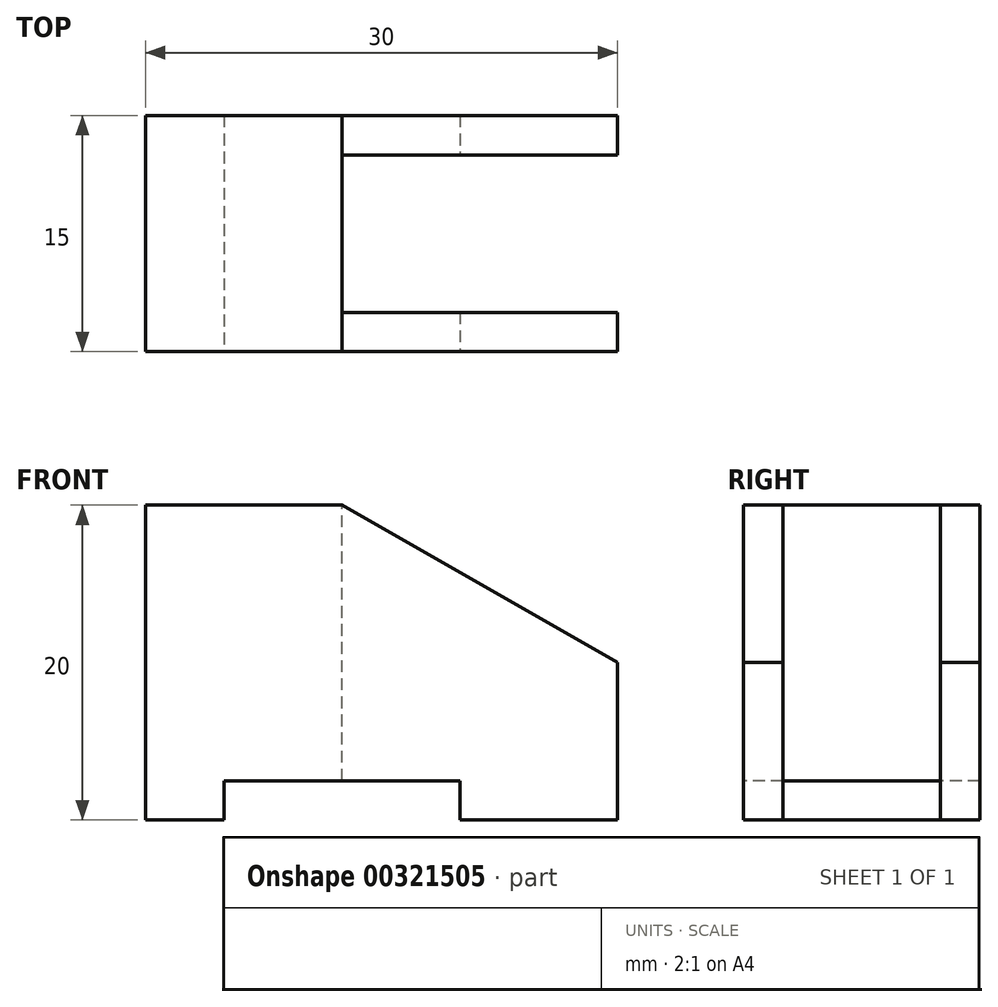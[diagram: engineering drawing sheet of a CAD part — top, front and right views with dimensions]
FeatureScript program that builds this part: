
annotation { "Feature Type Name" : "Feature", "Feature Type Description" : "" }
export const myFeature = defineFeature(function(context is Context, id is Id, definition is map)
    precondition{}
    {
        {
            var Q0;
            Q0=qCreatedBy(makeId("Front.planeOp"),FACE);
            var sketch = newSketch(context, id + "F0", { "sketchPlane" : qUnion([Q0])});
            skLineSegment(sketch, "E0.bottom", {"start": v(0, 0) * mm, "end": v(12.5, 0) * mm});
            skLineSegment(sketch, "E0.top", {"start": v(0, 20) * mm, "end": v(12.5, 20) * mm});
            skLineSegment(sketch, "E0.left", {"start": v(0, 0) * mm, "end": v(0, 20) * mm});
            skLineSegment(sketch, "E0.right", {"start": v(12.5, 0) * mm, "end": v(12.5, 20) * mm});
            skSolve(sketch);
        }
        {
            var Q0;
            Q0 = qSketchRegion(id + "F0", true);
            extrude(context, id + "F1", {"entities" : qUnion([Q0]), "endBound" : BoundingType.SYMMETRIC, "depth" : 15 * mm});
        }
        {
            var Q0;
            Q0=makeQuery(id+"F1.opExtrude","CAP_FACE",FACE,{"disambiguationData":[OSD([sQuery(id+"F0.wireOp",EDGE,"E0.bottom"),sQuery(id+"F0.wireOp",EDGE,"E0.top"),sQuery(id+"F0.wireOp",EDGE,"E0.left"),sQuery(id+"F0.wireOp",EDGE,"E0.right")])],"isStart":false});
            var sketch = newSketch(context, id + "F2", { "sketchPlane" : qUnion([Q0])});
            skLineSegment(sketch, "E1", {"start": v(12.5, 0) * mm, "end": v(30, 0) * mm});
            skLineSegment(sketch, "E2", {"start": v(30, 0) * mm, "end": v(30, 10) * mm});
            skLineSegment(sketch, "E3", {"start": v(30, 10) * mm, "end": v(12.5, 20) * mm});
            skSolve(sketch);
        }
        {
            var Q0;
            Q0 = qSketchRegion(id + "F2", true);
            var Q1;
            Q1=makeQuery(id+"F2.imprint","IMPRINT",FACE,{"disambiguationData":[TD([[makeQuery(id+"F2.imprint","IMPRINT",EDGE,{"derivedFrom":sQuery(id+"F2.wireOp",EDGE,"E1")}),1.0]])]});
            extrude(context, id + "F3", {"entities" : qUnion([Q0, Q1]), "operationType" : NewBodyOperationType.ADD, "oppositeDirection" : true, "depth" : 2.5 * mm});
        }
        {
            var Q0;
            Q0=makeQuery(id+"F1.opExtrude","CAP_FACE",FACE,{"disambiguationData":[OSD([sQuery(id+"F0.wireOp",EDGE,"E0.bottom"),sQuery(id+"F0.wireOp",EDGE,"E0.top"),sQuery(id+"F0.wireOp",EDGE,"E0.left"),sQuery(id+"F0.wireOp",EDGE,"E0.right")])],"isStart":true});
            var sketch = newSketch(context, id + "F4", { "sketchPlane" : qUnion([Q0])});
            skLineSegment(sketch, "E4", {"start": v(-12.5, 0) * mm, "end": v(-30, 0) * mm});
            skLineSegment(sketch, "E5", {"start": v(-30, 0) * mm, "end": v(-30, 10) * mm});
            skLineSegment(sketch, "E6", {"start": v(-30, 10) * mm, "end": v(-12.5, 20) * mm});
            skLineSegment(sketch, "E7", {"start": v(-12.5, 20) * mm, "end": v(-12.5, 0) * mm});
            skSolve(sketch);
        }
        {
            var Q0;
            Q0=makeQuery(id+"F4.imprint","IMPRINT",FACE,{"disambiguationData":[TD([[makeQuery(id+"F4.imprint","IMPRINT",EDGE,{"derivedFrom":sQuery(id+"F4.wireOp",EDGE,"E4")}),-1.0]])]});
            extrude(context, id + "F5", {"entities" : qUnion([Q0]), "operationType" : NewBodyOperationType.ADD, "oppositeDirection" : true, "depth" : 2.5 * mm});
        }
        {
            var Q0;
            {var subQ0=sQuery(id+"F0.wireOp",EDGE,"E0.right");Q0=makeQuery(id+"F3.boolean.opBoolean","MERGE",FACE,{"derivedFrom":[makeQuery(id+"F1.opExtrude","CAP_FACE",FACE,{"disambiguationData":[OSD([sQuery(id+"F0.wireOp",EDGE,"E0.bottom"),sQuery(id+"F0.wireOp",EDGE,"E0.top"),sQuery(id+"F0.wireOp",EDGE,"E0.left"),subQ0])],"isStart":false}),makeQuery(id+"F3.opExtrude","CAP_FACE",FACE,{"disambiguationData":[OSD([subQ0,sQuery(id+"F2.wireOp",EDGE,"E1"),sQuery(id+"F2.wireOp",EDGE,"E2"),sQuery(id+"F2.wireOp",EDGE,"E3")])],"isStart":true})]});}
            var sketch = newSketch(context, id + "F6", { "sketchPlane" : qUnion([Q0])});
            skLineSegment(sketch, "E8.bottom", {"start": v(5, 0) * mm, "end": v(20, 0) * mm});
            skLineSegment(sketch, "E8.top", {"start": v(5, 2.5) * mm, "end": v(20, 2.5) * mm});
            skLineSegment(sketch, "E8.left", {"start": v(5, 0) * mm, "end": v(5, 2.5) * mm});
            skLineSegment(sketch, "E8.right", {"start": v(20, 0) * mm, "end": v(20, 2.5) * mm});
            skSolve(sketch);
        }
        {
            var Q0;
            Q0=makeQuery(id+"F6.imprint","IMPRINT",FACE,{"disambiguationData":[TD([[makeQuery(id+"F6.imprint","IMPRINT",EDGE,{"derivedFrom":sQuery(id+"F6.wireOp",EDGE,"E8.bottom")}),1.0]])]});
            var Q1;
            Q1=makeQuery(id+"F5.boolean.opBoolean","MERGE",FACE,{"derivedFrom":[makeQuery(id+"F1.opExtrude","CAP_FACE",FACE,{"disambiguationData":[OSD([sQuery(id+"F0.wireOp",EDGE,"E0.bottom"),sQuery(id+"F0.wireOp",EDGE,"E0.top"),sQuery(id+"F0.wireOp",EDGE,"E0.left"),sQuery(id+"F0.wireOp",EDGE,"E0.right")])],"isStart":true}),makeQuery(id+"F5.opExtrude","CAP_FACE",FACE,{"disambiguationData":[OSD([sQuery(id+"F4.wireOp",EDGE,"E4"),sQuery(id+"F4.wireOp",EDGE,"E5"),sQuery(id+"F4.wireOp",EDGE,"E6"),sQuery(id+"F4.wireOp",EDGE,"E7")])],"isStart":true})]});
            extrude(context, id + "F7", {"entities" : qUnion([Q0]), "operationType" : NewBodyOperationType.REMOVE, "endBound" : BoundingType.UP_TO_SURFACE, "oppositeDirection" : true, "endBoundEntityFace" : qUnion([Q1]), "depth" : 25 * mm});
        }
    });
